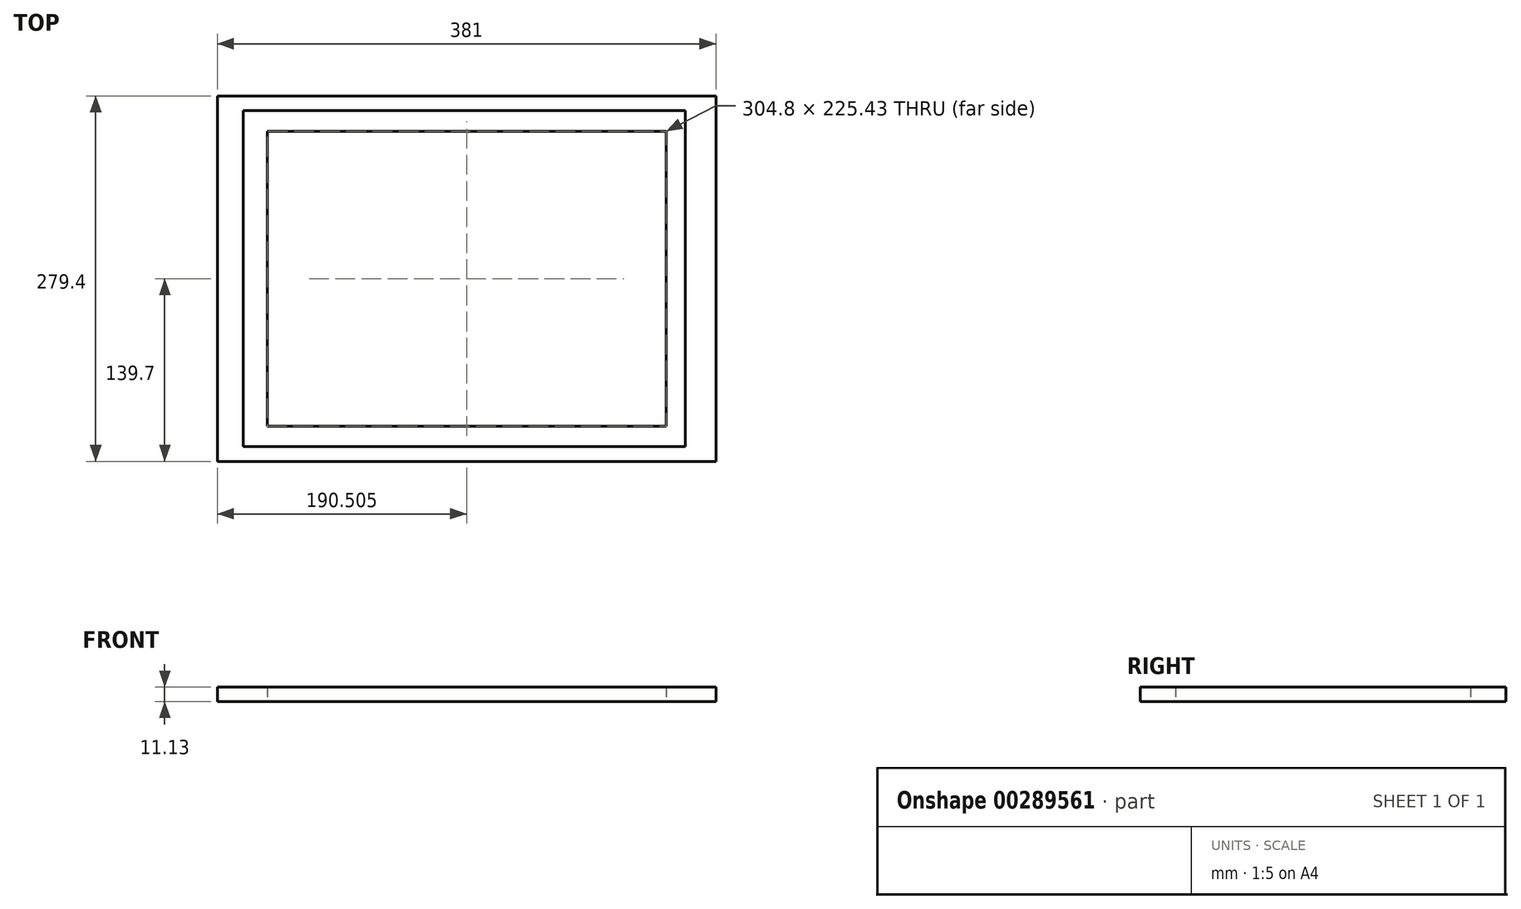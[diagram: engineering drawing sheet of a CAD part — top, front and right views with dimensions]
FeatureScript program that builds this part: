
annotation { "Feature Type Name" : "Feature", "Feature Type Description" : "" }
export const myFeature = defineFeature(function(context is Context, id is Id, definition is map)
    precondition{}
    {
        {
            var Q0;
            Q0=qCreatedBy(makeId("Top.planeOp"),FACE);
            var sketch = newSketch(context, id + "F0", { "sketchPlane" : qUnion([Q0])});
            skLineSegment(sketch, "E0.bottom", {"start": v(-188.08, 99.1) * mm, "end": v(192.92, 99.1) * mm});
            skLineSegment(sketch, "E0.top", {"start": v(-188.08, -180.3) * mm, "end": v(192.92, -180.3) * mm});
            skLineSegment(sketch, "E0.left", {"start": v(-188.08, 99.1) * mm, "end": v(-188.08, -180.3) * mm});
            skLineSegment(sketch, "E0.right", {"start": v(192.92, 99.1) * mm, "end": v(192.92, -180.3) * mm});
            skLineSegment(sketch, "E1.bottom", {"start": v(-149.98, 72.11) * mm, "end": v(154.82, 72.11) * mm});
            skLineSegment(sketch, "E1.top", {"start": v(-149.98, -153.31) * mm, "end": v(154.82, -153.31) * mm});
            skLineSegment(sketch, "E1.left", {"start": v(-149.98, 72.11) * mm, "end": v(-149.98, -153.31) * mm});
            skLineSegment(sketch, "E1.right", {"start": v(154.82, 72.11) * mm, "end": v(154.82, -153.31) * mm});
            skSolve(sketch);
        }
        {
            var Q0;
            Q0 = qSketchRegion(id + "F0", true);
            extrude(context, id + "F1", {"entities" : qUnion([Q0]), "depth" : 11.1 * mm});
        }
        {
            var Q0;
            Q0=makeQuery(id+"F1.opExtrude","CAP_FACE",FACE,{"disambiguationData":[OSD([sQuery(id+"F0.wireOp",EDGE,"E0.bottom"),sQuery(id+"F0.wireOp",EDGE,"E0.top"),sQuery(id+"F0.wireOp",EDGE,"E0.left"),sQuery(id+"F0.wireOp",EDGE,"E0.right"),sQuery(id+"F0.wireOp",EDGE,"E1.bottom"),sQuery(id+"F0.wireOp",EDGE,"E1.top"),sQuery(id+"F0.wireOp",EDGE,"E1.left"),sQuery(id+"F0.wireOp",EDGE,"E1.right")])],"isStart":false});
            var sketch = newSketch(context, id + "F2", { "sketchPlane" : qUnion([Q0])});
            skLineSegment(sketch, "E2.bottom", {"start": v(-168.14, 87.8) * mm, "end": v(169.43, 87.8) * mm});
            skLineSegment(sketch, "E2.top", {"start": v(-168.14, -169) * mm, "end": v(169.43, -169) * mm});
            skLineSegment(sketch, "E2.left", {"start": v(-168.14, 87.8) * mm, "end": v(-168.14, -169) * mm});
            skLineSegment(sketch, "E2.right", {"start": v(169.43, 87.8) * mm, "end": v(169.43, -169) * mm});
            skLineSegment(sketch, "E3.bottom", {"start": v(-149.98, 72.11) * mm, "end": v(154.82, 72.11) * mm});
            skLineSegment(sketch, "E3.top", {"start": v(-149.98, -153.31) * mm, "end": v(154.82, -153.31) * mm});
            skLineSegment(sketch, "E3.left", {"start": v(-149.98, 72.11) * mm, "end": v(-149.98, -153.31) * mm});
            skLineSegment(sketch, "E3.right", {"start": v(154.82, 72.11) * mm, "end": v(154.82, -153.31) * mm});
            skSolve(sketch);
        }
        {
            var Q0;
            Q0 = qSketchRegion(id + "F2", true);
            extrude(context, id + "F3", {"entities" : qUnion([Q0]), "operationType" : NewBodyOperationType.ADD, "depth" : 7 / 406.4 * mm});
        }
    });
